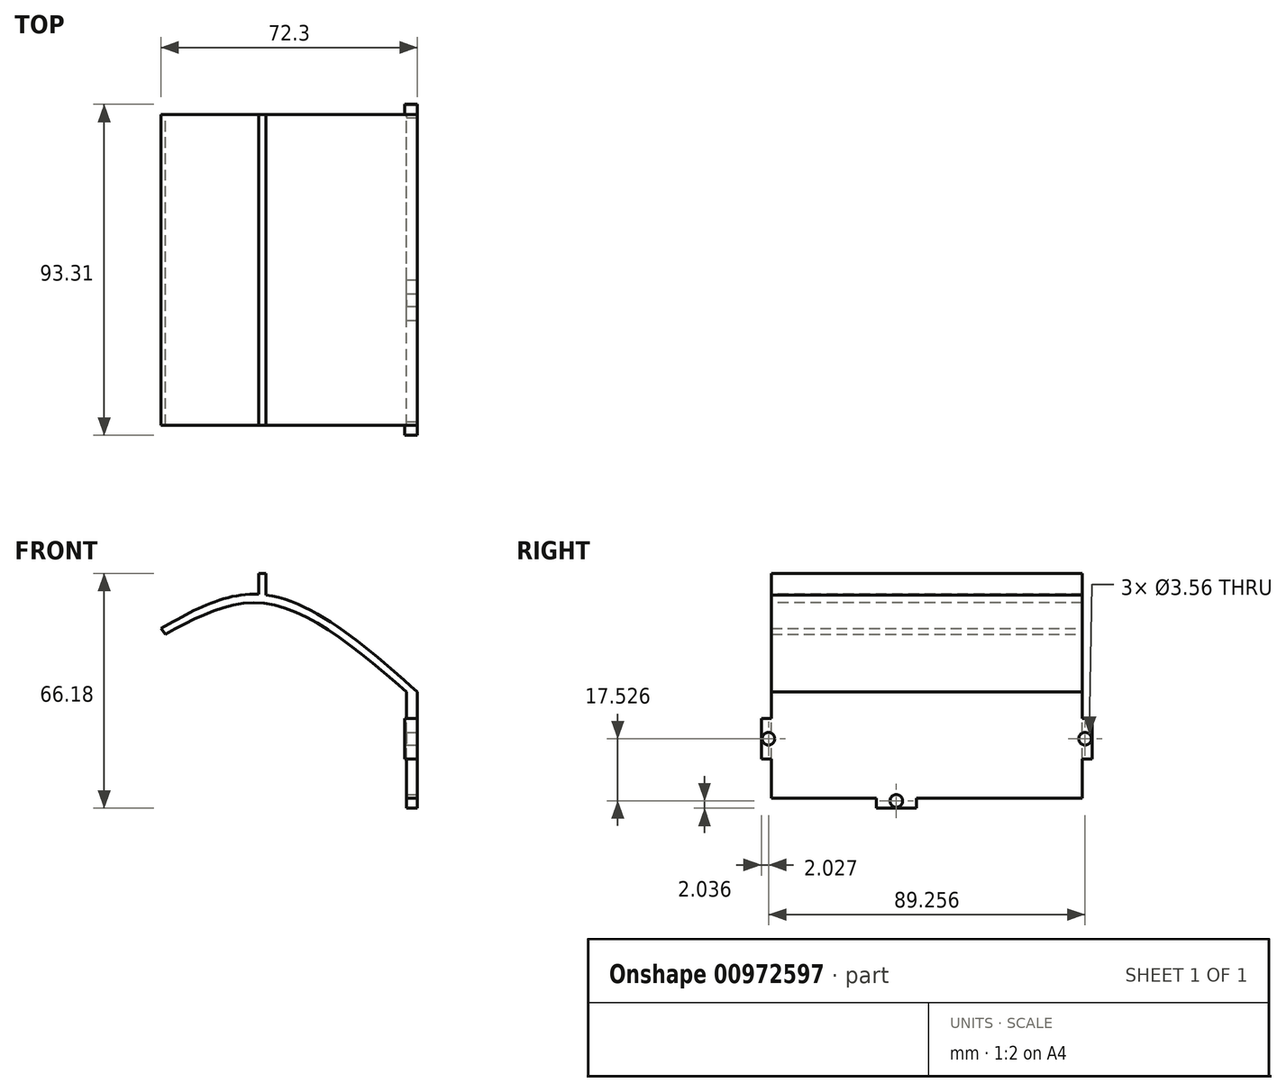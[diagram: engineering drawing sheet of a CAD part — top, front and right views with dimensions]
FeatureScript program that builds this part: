
annotation { "Feature Type Name" : "Feature", "Feature Type Description" : "" }
export const myFeature = defineFeature(function(context is Context, id is Id, definition is map)
    precondition{}
    {
        {
            var Q0;
            Q0=qCreatedBy(makeId("Front.planeOp"),FACE);
            var sketch = newSketch(context, id + "F0", { "sketchPlane" : qUnion([Q0])});
            skFitSpline(sketch, "E0", {"points": [v(-69.25, 47.29) * mm, v(-39.62, 56.74) * mm, v(3.05, 29.4) * mm], "startDerivative": vector(65.33, 36.76) * mm, "endDerivative": vector(75.68, -67.75) * mm});
            skLineSegment(sketch, "E1", {"start": v(3.05, 29.4) * mm, "end": v(3.05, -0.54) * mm});
            skLineSegment(sketch, "E2", {"start": v(3.05, -0.54) * mm, "end": v(0, -0.54) * mm});
            skLineSegment(sketch, "E3", {"start": v(0, -0.54) * mm, "end": v(0, 29.4) * mm});
            skFitSpline(sketch, "E4", {"points": [v(0, 29.4) * mm, v(-39.62, 54.35) * mm, v(-67.95, 45.66) * mm], "startDerivative": vector(-73.15, 62.71) * mm, "endDerivative": vector(-62.34, -33.87) * mm});
            skLineSegment(sketch, "E5", {"start": v(-67.95, 45.66) * mm, "end": v(-69.25, 47.29) * mm});
            skLineSegment(sketch, "E6", {"start": v(3.05, 29.4) * mm, "end": v(0, 29.4) * mm});
            skLineSegment(sketch, "E7", {"start": v(-39.62, 56.74) * mm, "end": v(-39.62, 62.79) * mm});
            skLineSegment(sketch, "E8", {"start": v(-39.62, 62.79) * mm, "end": v(-41.68, 62.79) * mm});
            skLineSegment(sketch, "E9", {"start": v(-41.68, 62.79) * mm, "end": v(-41.68, 56.92) * mm});
            skSolve(sketch);
        }
        {
            var Q0;
            Q0 = qSketchRegion(id + "F0", true);
            extrude(context, id + "F1", {"entities" : qUnion([Q0]), "depth" : 87.63 * mm, "offsetDistance" : 25.4 * mm});
        }
        {
            var Q0;
            Q0=makeQuery(id+"F1.opExtrude","SWEPT_FACE",FACE,{"disambiguationData":[OSD([sQuery(id+"F0.wireOp",EDGE,"E1")])]});
            var sketch = newSketch(context, id + "F2", { "sketchPlane" : qUnion([Q0])});
            skLineSegment(sketch, "E10", {"start": v(-87.63, -0.54) * mm, "end": v(-58.09, -0.54) * mm});
            skLineSegment(sketch, "E11", {"start": v(-58.09, -0.54) * mm, "end": v(-58.09, -3.39) * mm});
            skLineSegment(sketch, "E12", {"start": v(-58.09, -3.39) * mm, "end": v(-46.71, -3.39) * mm});
            skLineSegment(sketch, "E13", {"start": v(-46.71, -3.39) * mm, "end": v(-46.71, -0.54) * mm});
            skCircle(sketch, "E14", {"center": v(-52.4, -1.35) * mm, "radius": 1.78 * mm});
            skLineSegment(sketch, "E15", {"start": v(-87.63, 10.48) * mm, "end": v(-90.47, 10.48) * mm});
            skLineSegment(sketch, "E16", {"start": v(-90.47, 10.48) * mm, "end": v(-90.47, 21.86) * mm});
            skLineSegment(sketch, "E17", {"start": v(-90.47, 21.86) * mm, "end": v(-87.63, 21.86) * mm});
            skCircle(sketch, "E18", {"center": v(-88.44, 16.17) * mm, "radius": 1.78 * mm});
            skLineSegment(sketch, "E19", {"start": v(0, 10.48) * mm, "end": v(2.84, 10.48) * mm});
            skLineSegment(sketch, "E20", {"start": v(2.84, 10.48) * mm, "end": v(2.84, 21.86) * mm});
            skLineSegment(sketch, "E21", {"start": v(2.84, 21.86) * mm, "end": v(0, 21.86) * mm});
            skCircle(sketch, "E22", {"center": v(0.81, 16.17) * mm, "radius": 1.78 * mm});
            skSolve(sketch);
        }
        {
            var Q0;
            Q0 = qSketchRegion(id + "F2", true);
            var Q1;
            {var subQ1=sQuery(id+"F2.wireOp",EDGE,"E11");Q1=makeQuery(id+"F2.imprint","IMPRINT",FACE,{"disambiguationData":[TD([[makeQuery(id+"F2.imprint","IMPRINT",EDGE,{"derivedFrom":subQ1}),1.0]])]});}
            var Q2;
            {var subQ1=sQuery(id+"F2.wireOp",EDGE,"E11");Q2=makeQuery(id+"F2.imprint","IMPRINT",FACE,{"disambiguationData":[TD([[makeQuery(id+"F2.imprint","IMPRINT",EDGE,{"derivedFrom":subQ1}),1.0]])]});}
            extrude(context, id + "F3", {"entities" : qUnion([Q0, Q1, Q2]), "operationType" : NewBodyOperationType.ADD, "oppositeDirection" : true, "depth" : 3.05 * mm, "offsetDistance" : 25.4 * mm});
        }
        {
            var Q0;
            Q0=makeQuery(id+"F2.imprint","IMPRINT",FACE,{"disambiguationData":[TD([[makeQuery(id+"F2.imprint","IMPRINT",EDGE,{"derivedFrom":sQuery(id+"F2.wireOp",EDGE,"E14")}),1.0]])]});
            extrude(context, id + "F4", {"entities" : qUnion([Q0]), "operationType" : NewBodyOperationType.REMOVE, "oppositeDirection" : true, "depth" : 25.4 * mm, "offsetDistance" : 25.4 * mm});
        }
        {
            var Q0;
            Q0 = qSketchRegion(id + "F2", true);
            var Q1;
            {var subQ0=sQuery(id+"F2.wireOp",EDGE,"E18");var subQ1=makeQuery(id+"F1.opExtrude","CAP_EDGE",EDGE,{"disambiguationData":[OSD([sQuery(id+"F0.wireOp",EDGE,"E1")])],"isStart":false});var subQ2=makeQuery(id+"F2.imprint","INTERSECT",VERTEX,{"disambiguationData":[OD(0.0)],"derivedFrom":[subQ1,subQ0]});Q1=makeQuery(id+"F2.imprint","IMPRINT",FACE,{"disambiguationData":[TD([[makeQuery(id+"F2.imprint","IMPRINT",EDGE,{"disambiguationData":[TD([[subQ2,1.0]])],"derivedFrom":subQ0}),1.0]])]});}
            extrude(context, id + "F5", {"entities" : qUnion([Q0, Q1]), "operationType" : NewBodyOperationType.REMOVE, "oppositeDirection" : true, "depth" : 25.4 * mm, "offsetDistance" : 25.4 * mm});
        }
        {
            var Q0;
            {var subQ5=sQuery(id+"F2.wireOp",EDGE,"E15");Q0=makeQuery(id+"F2.imprint","IMPRINT",FACE,{"disambiguationData":[TD([[makeQuery(id+"F2.imprint","IMPRINT",EDGE,{"derivedFrom":subQ5}),-1.0]])]});}
            extrude(context, id + "F6", {"entities" : qUnion([Q0]), "operationType" : NewBodyOperationType.ADD, "oppositeDirection" : true, "depth" : 3.56 * mm, "offsetDistance" : 25.4 * mm});
        }
        {
            var Q0;
            {var subQ5=sQuery(id+"F2.wireOp",EDGE,"E19");Q0=makeQuery(id+"F2.imprint","IMPRINT",FACE,{"disambiguationData":[TD([[makeQuery(id+"F2.imprint","IMPRINT",EDGE,{"derivedFrom":subQ5}),1.0]])]});}
            extrude(context, id + "F7", {"entities" : qUnion([Q0]), "operationType" : NewBodyOperationType.ADD, "oppositeDirection" : true, "depth" : 3.56 * mm, "offsetDistance" : 25.4 * mm});
        }
    });
